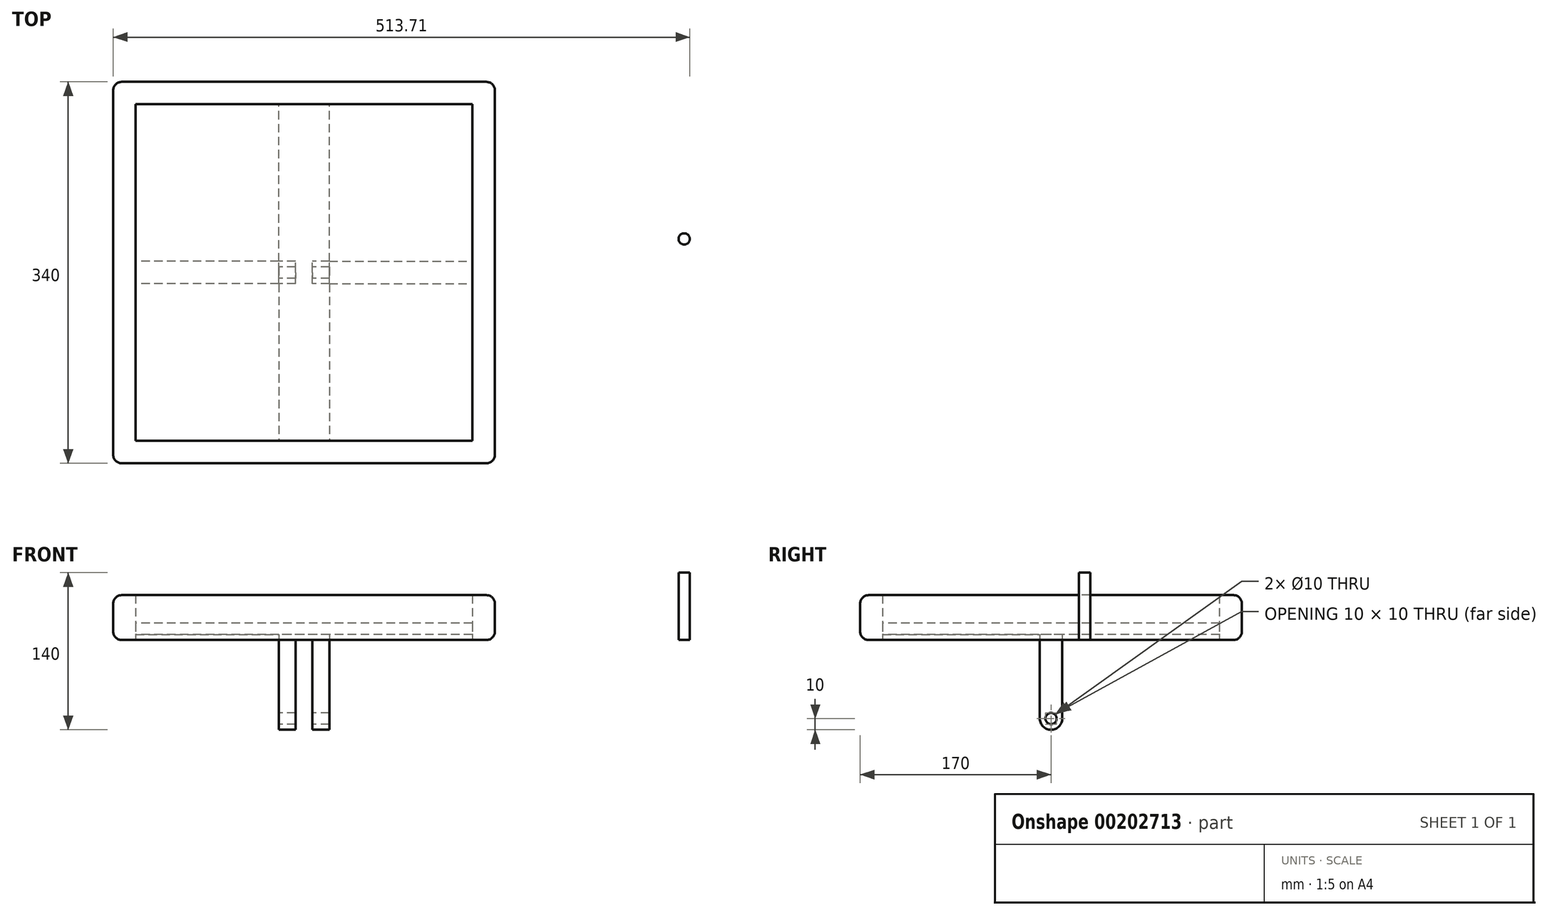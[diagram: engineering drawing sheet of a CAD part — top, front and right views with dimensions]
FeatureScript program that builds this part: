
annotation { "Feature Type Name" : "Feature", "Feature Type Description" : "" }
export const myFeature = defineFeature(function(context is Context, id is Id, definition is map)
    precondition{}
    {
        {
            var Q0;
            Q0=qCreatedBy(makeId("Top.planeOp"),FACE);
            var sketch = newSketch(context, id + "F0", { "sketchPlane" : qUnion([Q0])});
            skLineSegment(sketch, "E0.bottom", {"start": v(170, 170) * mm, "end": v(-170, 170) * mm});
            skLineSegment(sketch, "E0.top", {"start": v(170, -170) * mm, "end": v(-170, -170) * mm});
            skLineSegment(sketch, "E0.left", {"start": v(170, 170) * mm, "end": v(170, -170) * mm});
            skLineSegment(sketch, "E0.right", {"start": v(-170, 170) * mm, "end": v(-170, -170) * mm});
            skPoint(sketch, "E0.middle", {"position": v(0, 0) * mm});
            skLineSegment(sketch, "E1.bottom", {"start": v(150, 150) * mm, "end": v(-150, 150) * mm});
            skLineSegment(sketch, "E1.top", {"start": v(150, -150) * mm, "end": v(-150, -150) * mm});
            skLineSegment(sketch, "E1.left", {"start": v(150, 150) * mm, "end": v(150, -150) * mm});
            skLineSegment(sketch, "E1.right", {"start": v(-150, 150) * mm, "end": v(-150, -150) * mm});
            skCircle(sketch, "E2", {"center": v(338.71, 30.01) * mm, "radius": 5 * mm});
            skSolve(sketch);
        }
        {
            var Q0;
            Q0=makeQuery(id+"F0.imprint","IMPRINT",FACE,{"disambiguationData":[TD([[makeQuery(id+"F0.imprint","IMPRINT",EDGE,{"derivedFrom":sQuery(id+"F0.wireOp",EDGE,"E0.bottom")}),1.0]])]});
            extrude(context, id + "F1", {"entities" : qUnion([Q0]), "depth" : 40 * mm});
        }
        {
            var Q0;
            Q0=makeQuery(id+"F0.imprint","IMPRINT",FACE,{"disambiguationData":[TD([[makeQuery(id+"F0.imprint","IMPRINT",EDGE,{"derivedFrom":sQuery(id+"F0.wireOp",EDGE,"E1.bottom")}),1.0]])]});
            extrude(context, id + "F2", {"entities" : qUnion([Q0]), "operationType" : NewBodyOperationType.ADD, "depth" : 5 * mm});
        }
        {
            var Q0;
            Q0=makeQuery(id+"F0.imprint","IMPRINT",FACE,{"disambiguationData":[TD([[makeQuery(id+"F0.imprint","IMPRINT",EDGE,{"derivedFrom":sQuery(id+"F0.wireOp",EDGE,"E1.bottom")}),1.0]])]});
            var sketch = newSketch(context, id + "F3", { "sketchPlane" : qUnion([Q0])});
            skLineSegment(sketch, "E3.bottom", {"start": v(7.5, -10) * mm, "end": v(-7.5, -10) * mm});
            skLineSegment(sketch, "E3.top", {"start": v(7.5, 10) * mm, "end": v(-7.5, 10) * mm});
            skLineSegment(sketch, "E3.left", {"start": v(7.5, -10) * mm, "end": v(7.5, 10) * mm});
            skLineSegment(sketch, "E3.right", {"start": v(-7.5, -10) * mm, "end": v(-7.5, 10) * mm});
            skPoint(sketch, "E3.middle", {"position": v(0, 0) * mm});
            skLineSegment(sketch, "E4.bottom", {"start": v(22.5, -10) * mm, "end": v(-22.5, -10) * mm});
            skLineSegment(sketch, "E4.top", {"start": v(22.5, 10) * mm, "end": v(-22.5, 10) * mm});
            skLineSegment(sketch, "E4.left", {"start": v(22.5, -10) * mm, "end": v(22.5, 10) * mm});
            skLineSegment(sketch, "E4.right", {"start": v(-22.5, -10) * mm, "end": v(-22.5, 10) * mm});
            skLineSegment(sketch, "E5.bottom", {"start": v(-22.5, 10) * mm, "end": v(-150, 10) * mm});
            skLineSegment(sketch, "E5.top", {"start": v(-22.5, 150) * mm, "end": v(-150, 150) * mm});
            skLineSegment(sketch, "E5.left", {"start": v(-22.5, 10) * mm, "end": v(-22.5, 150) * mm});
            skLineSegment(sketch, "E5.right", {"start": v(-150, 10) * mm, "end": v(-150, 150) * mm});
            skLineSegment(sketch, "E6.bottom", {"start": v(22.5, 10) * mm, "end": v(150, 10) * mm});
            skLineSegment(sketch, "E6.top", {"start": v(22.5, 150) * mm, "end": v(150, 150) * mm});
            skLineSegment(sketch, "E6.left", {"start": v(22.5, 10) * mm, "end": v(22.5, 150) * mm});
            skLineSegment(sketch, "E6.right", {"start": v(150, 10) * mm, "end": v(150, 150) * mm});
            skLineSegment(sketch, "E7.bottom", {"start": v(22.5, -10) * mm, "end": v(150, -10) * mm});
            skLineSegment(sketch, "E7.top", {"start": v(22.5, -150) * mm, "end": v(150, -150) * mm});
            skLineSegment(sketch, "E7.left", {"start": v(22.5, -10) * mm, "end": v(22.5, -150) * mm});
            skLineSegment(sketch, "E7.right", {"start": v(150, -10) * mm, "end": v(150, -150) * mm});
            skLineSegment(sketch, "E8.bottom", {"start": v(-22.5, -10) * mm, "end": v(-150, -10) * mm});
            skLineSegment(sketch, "E8.top", {"start": v(-22.5, -150) * mm, "end": v(-150, -150) * mm});
            skLineSegment(sketch, "E8.left", {"start": v(-22.5, -10) * mm, "end": v(-22.5, -150) * mm});
            skLineSegment(sketch, "E8.right", {"start": v(-150, -10) * mm, "end": v(-150, -150) * mm});
            skSolve(sketch);
        }
        {
            var Q0;
            {var subQ0=sQuery(id+"F3.wireOp",EDGE,"E3.left");Q0=makeQuery(id+"F3.imprint","IMPRINT",FACE,{"disambiguationData":[TD([[makeQuery(id+"F3.imprint","IMPRINT",EDGE,{"derivedFrom":subQ0}),-1.0]])]});}
            var Q1;
            {var subQ0=sQuery(id+"F3.wireOp",EDGE,"E3.right");Q1=makeQuery(id+"F3.imprint","IMPRINT",FACE,{"disambiguationData":[TD([[makeQuery(id+"F3.imprint","IMPRINT",EDGE,{"derivedFrom":subQ0}),1.0]])]});}
            extrude(context, id + "F4", {"entities" : qUnion([Q0, Q1]), "operationType" : NewBodyOperationType.ADD, "oppositeDirection" : true, "depth" : 80 * mm});
        }
        {
            var Q0;
            {var subQ0=sQuery(id+"F3.wireOp",EDGE,"E4.bottom");Q0=makeQuery(id+"F4.opExtrude","CAP_EDGE",EDGE,{"disambiguationData":[OSD([subQ0]),TDD([makeQuery(id+"F3.imprint","IMPRINT",EDGE,{"disambiguationData":[TD([[makeQuery(id+"F3.imprint","INTERSECT",VERTEX,{"derivedFrom":[sQuery(id+"F3.wireOp",EDGE,"E3.right"),subQ0]}),-1.0]])],"derivedFrom":subQ0})])],"isStart":false});}
            var Q1;
            {var subQ0=sQuery(id+"F3.wireOp",EDGE,"E4.top");Q1=makeQuery(id+"F4.opExtrude","CAP_EDGE",EDGE,{"disambiguationData":[OSD([subQ0]),TDD([makeQuery(id+"F3.imprint","IMPRINT",EDGE,{"disambiguationData":[TD([[makeQuery(id+"F3.imprint","INTERSECT",VERTEX,{"derivedFrom":[sQuery(id+"F3.wireOp",EDGE,"E3.right"),subQ0]}),-1.0]])],"derivedFrom":subQ0})])],"isStart":false});}
            var Q2;
            {var subQ0=sQuery(id+"F3.wireOp",EDGE,"E4.bottom");Q2=makeQuery(id+"F4.opExtrude","CAP_EDGE",EDGE,{"disambiguationData":[OSD([subQ0]),TDD([makeQuery(id+"F3.imprint","IMPRINT",EDGE,{"disambiguationData":[TD([[makeQuery(id+"F3.imprint","INTERSECT",VERTEX,{"derivedFrom":[sQuery(id+"F3.wireOp",EDGE,"E3.left"),subQ0]}),1.0]])],"derivedFrom":subQ0})])],"isStart":false});}
            var Q3;
            {var subQ0=sQuery(id+"F3.wireOp",EDGE,"E4.top");Q3=makeQuery(id+"F4.opExtrude","CAP_EDGE",EDGE,{"disambiguationData":[OSD([subQ0]),TDD([makeQuery(id+"F3.imprint","IMPRINT",EDGE,{"disambiguationData":[TD([[makeQuery(id+"F3.imprint","INTERSECT",VERTEX,{"derivedFrom":[sQuery(id+"F3.wireOp",EDGE,"E3.left"),subQ0]}),1.0]])],"derivedFrom":subQ0})])],"isStart":false});}
            fillet(context, id + "F5", {"entities" : qUnion([Q0, Q1, Q2, Q3]), "radius" : 10 * mm, "tangentPropagation" : true, "allowEdgeOverflow" : false});
        }
        {
            var Q0;
            Q0=makeQuery(id+"F1.opExtrude","SWEPT_EDGE",EDGE,{"disambiguationData":[OSD([sQuery(id+"F0.wireOp",EDGE,"E0.top"),sQuery(id+"F0.wireOp",EDGE,"E0.right")])]});
            var Q1;
            Q1=makeQuery(id+"F1.opExtrude","SWEPT_EDGE",EDGE,{"disambiguationData":[OSD([sQuery(id+"F0.wireOp",EDGE,"E0.top"),sQuery(id+"F0.wireOp",EDGE,"E0.left")])]});
            var Q2;
            Q2=makeQuery(id+"F1.opExtrude","SWEPT_EDGE",EDGE,{"disambiguationData":[OSD([sQuery(id+"F0.wireOp",EDGE,"E0.bottom"),sQuery(id+"F0.wireOp",EDGE,"E0.right")])]});
            var Q3;
            Q3=makeQuery(id+"F1.opExtrude","CAP_EDGE",EDGE,{"disambiguationData":[OSD([sQuery(id+"F0.wireOp",EDGE,"E0.bottom")])],"isStart":true});
            var Q4;
            Q4=makeQuery(id+"F1.opExtrude","CAP_EDGE",EDGE,{"disambiguationData":[OSD([sQuery(id+"F0.wireOp",EDGE,"E0.left")])],"isStart":true});
            var Q5;
            Q5=makeQuery(id+"F1.opExtrude","SWEPT_EDGE",EDGE,{"disambiguationData":[OSD([sQuery(id+"F0.wireOp",EDGE,"E0.bottom"),sQuery(id+"F0.wireOp",EDGE,"E0.left")])]});
            var Q6;
            Q6=makeQuery(id+"F1.opExtrude","CAP_EDGE",EDGE,{"disambiguationData":[OSD([sQuery(id+"F0.wireOp",EDGE,"E0.left")])],"isStart":false});
            var Q7;
            Q7=makeQuery(id+"F1.opExtrude","CAP_EDGE",EDGE,{"disambiguationData":[OSD([sQuery(id+"F0.wireOp",EDGE,"E0.top")])],"isStart":false});
            var Q8;
            Q8=makeQuery(id+"F1.opExtrude","CAP_EDGE",EDGE,{"disambiguationData":[OSD([sQuery(id+"F0.wireOp",EDGE,"E0.top")])],"isStart":true});
            var Q9;
            Q9=makeQuery(id+"F1.opExtrude","CAP_EDGE",EDGE,{"disambiguationData":[OSD([sQuery(id+"F0.wireOp",EDGE,"E0.right")])],"isStart":false});
            var Q10;
            Q10=makeQuery(id+"F1.opExtrude","CAP_EDGE",EDGE,{"disambiguationData":[OSD([sQuery(id+"F0.wireOp",EDGE,"E0.right")])],"isStart":true});
            var Q11;
            Q11=makeQuery(id+"F1.opExtrude","CAP_EDGE",EDGE,{"disambiguationData":[OSD([sQuery(id+"F0.wireOp",EDGE,"E0.bottom")])],"isStart":false});
            fillet(context, id + "F6", {"entities" : qUnion([Q0, Q1, Q2, Q3, Q4, Q5, Q6, Q7, Q8, Q9, Q10, Q11]), "radius" : 7.5 * mm, "tangentPropagation" : true, "allowEdgeOverflow" : false});
        }
        {
            var Q0;
            Q0=makeQuery(id+"F4.opExtrude","SWEPT_FACE",FACE,{"disambiguationData":[OSD([sQuery(id+"F3.wireOp",EDGE,"E4.right")])]});
            var sketch = newSketch(context, id + "F7", { "sketchPlane" : qUnion([Q0])});
            skCircle(sketch, "E9", {"center": v(0, -70) * mm, "radius": 5 * mm});
            skSolve(sketch);
        }
        {
            var Q0;
            Q0=makeQuery(id+"F7.imprint","IMPRINT",FACE,{"disambiguationData":[TD([[makeQuery(id+"F7.imprint","IMPRINT",EDGE,{"derivedFrom":sQuery(id+"F7.wireOp",EDGE,"E9")}),1.0]])]});
            extrude(context, id + "F8", {"entities" : qUnion([Q0]), "oppositeDirection" : true, "depth" : 45 * mm});
        }
        {
            var Q0;
            Q0=makeQuery(id+"F8.opExtrude","SWEPT_BODY",BODY,{"disambiguationData":[OSD([sQuery(id+"F7.wireOp",EDGE,"E9")])]});
            var Q1;
            Q1=makeQuery(id+"F1.opExtrude","SWEPT_BODY",BODY,{"disambiguationData":[OSD([sQuery(id+"F0.wireOp",EDGE,"E0.bottom"),sQuery(id+"F0.wireOp",EDGE,"E0.top"),sQuery(id+"F0.wireOp",EDGE,"E0.left"),sQuery(id+"F0.wireOp",EDGE,"E0.right"),sQuery(id+"F0.wireOp",EDGE,"E1.bottom"),sQuery(id+"F0.wireOp",EDGE,"E1.top"),sQuery(id+"F0.wireOp",EDGE,"E1.left"),sQuery(id+"F0.wireOp",EDGE,"E1.right")])]});
            booleanBodies(context, id + "F9", {"operationType" : BooleanOperationType.SUBTRACTION, "tools" : qUnion([Q0]), "targets" : qUnion([Q1])});
        }
        {
            var Q0;
            Q0=makeQuery(id+"F0.imprint","IMPRINT",FACE,{"disambiguationData":[TD([[makeQuery(id+"F0.imprint","IMPRINT",EDGE,{"derivedFrom":sQuery(id+"F0.wireOp",EDGE,"E2")}),1.0]])]});
            extrude(context, id + "F10", {"entities" : qUnion([Q0]), "depth" : 60 * mm});
        }
        {
            var Q0;
            Q0=makeQuery(id+"F3.imprint","IMPRINT",FACE,{"disambiguationData":[TD([[makeQuery(id+"F3.imprint","IMPRINT",EDGE,{"derivedFrom":sQuery(id+"F3.wireOp",EDGE,"E5.bottom")}),-1.0]])]});
            var Q1;
            Q1=makeQuery(id+"F3.imprint","IMPRINT",FACE,{"disambiguationData":[TD([[makeQuery(id+"F3.imprint","IMPRINT",EDGE,{"derivedFrom":sQuery(id+"F3.wireOp",EDGE,"E6.bottom")}),1.0]])]});
            var Q2;
            Q2=makeQuery(id+"F3.imprint","IMPRINT",FACE,{"disambiguationData":[TD([[makeQuery(id+"F3.imprint","IMPRINT",EDGE,{"derivedFrom":sQuery(id+"F3.wireOp",EDGE,"E7.bottom")}),-1.0]])]});
            var Q3;
            Q3=makeQuery(id+"F3.imprint","IMPRINT",FACE,{"disambiguationData":[TD([[makeQuery(id+"F3.imprint","IMPRINT",EDGE,{"derivedFrom":sQuery(id+"F3.wireOp",EDGE,"E8.bottom")}),1.0]])]});
            extrude(context, id + "F11", {"entities" : qUnion([Q0, Q1, Q2, Q3]), "operationType" : NewBodyOperationType.REMOVE, "endBound" : BoundingType.THROUGH_ALL, "depth" : 25 * mm});
        }
        {
            var Q0;
            Q0=makeQuery(id+"F2.opExtrude","CAP_FACE",FACE,{"disambiguationData":[OSD([sQuery(id+"F0.wireOp",EDGE,"E1.bottom"),sQuery(id+"F0.wireOp",EDGE,"E1.top"),sQuery(id+"F0.wireOp",EDGE,"E1.left"),sQuery(id+"F0.wireOp",EDGE,"E1.right")])],"isStart":false});
            var sketch = newSketch(context, id + "F12", { "sketchPlane" : qUnion([Q0])});
            skLineSegment(sketch, "E10.bottom", {"start": v(150, 150) * mm, "end": v(-150, 150) * mm});
            skLineSegment(sketch, "E10.top", {"start": v(150, -150) * mm, "end": v(-150, -150) * mm});
            skLineSegment(sketch, "E10.left", {"start": v(150, 150) * mm, "end": v(150, -150) * mm});
            skLineSegment(sketch, "E10.right", {"start": v(-150, 150) * mm, "end": v(-150, -150) * mm});
            skPoint(sketch, "E10.middle", {"position": v(0, 0) * mm});
            skSolve(sketch);
        }
        {
            var Q0;
            {var subQ1=makeQuery(id+"F2.opExtrude","CAP_FACE",FACE,{"disambiguationData":[OSD([sQuery(id+"F0.wireOp",EDGE,"E1.bottom"),sQuery(id+"F0.wireOp",EDGE,"E1.top"),sQuery(id+"F0.wireOp",EDGE,"E1.left"),sQuery(id+"F0.wireOp",EDGE,"E1.right")])],"isStart":false});var subQ5=makeQuery(id+"F11.boolean.opBoolean","INTERSECT",EDGE,{"derivedFrom":[subQ1,makeQuery(id+"F11.opExtrude","SWEPT_FACE",FACE,{"disambiguationData":[OSD([sQuery(id+"F3.wireOp",EDGE,"E8.bottom")])]})]});Q0=makeQuery(id+"F12.imprint","IMPRINT",FACE,{"disambiguationData":[TD([[makeQuery(id+"F12.imprint","IMPRINT",EDGE,{"derivedFrom":subQ5}),-1.0]])]});}
            var Q1;
            {var subQ0=makeQuery(id+"F2.opExtrude","CAP_FACE",FACE,{"disambiguationData":[OSD([sQuery(id+"F0.wireOp",EDGE,"E1.bottom"),sQuery(id+"F0.wireOp",EDGE,"E1.top"),sQuery(id+"F0.wireOp",EDGE,"E1.left"),sQuery(id+"F0.wireOp",EDGE,"E1.right")])],"isStart":false});var subQ2=makeQuery(id+"F11.boolean.opBoolean","INTERSECT",EDGE,{"derivedFrom":[subQ0,makeQuery(id+"F11.opExtrude","SWEPT_FACE",FACE,{"disambiguationData":[OSD([sQuery(id+"F3.wireOp",EDGE,"E5.bottom")])]})]});Q1=makeQuery(id+"F12.imprint","IMPRINT",FACE,{"disambiguationData":[TD([[makeQuery(id+"F12.imprint","IMPRINT",EDGE,{"derivedFrom":subQ2}),-1.0]])]});}
            var Q2;
            {var subQ1=makeQuery(id+"F2.opExtrude","CAP_FACE",FACE,{"disambiguationData":[OSD([sQuery(id+"F0.wireOp",EDGE,"E1.bottom"),sQuery(id+"F0.wireOp",EDGE,"E1.top"),sQuery(id+"F0.wireOp",EDGE,"E1.left"),sQuery(id+"F0.wireOp",EDGE,"E1.right")])],"isStart":false});var subQ5=makeQuery(id+"F11.boolean.opBoolean","INTERSECT",EDGE,{"derivedFrom":[subQ1,makeQuery(id+"F11.opExtrude","SWEPT_FACE",FACE,{"disambiguationData":[OSD([sQuery(id+"F3.wireOp",EDGE,"E5.bottom")])]})]});Q2=makeQuery(id+"F12.imprint","IMPRINT",FACE,{"disambiguationData":[TD([[makeQuery(id+"F12.imprint","IMPRINT",EDGE,{"derivedFrom":subQ5}),1.0]])]});}
            var Q3;
            {var subQ1=makeQuery(id+"F2.opExtrude","CAP_FACE",FACE,{"disambiguationData":[OSD([sQuery(id+"F0.wireOp",EDGE,"E1.bottom"),sQuery(id+"F0.wireOp",EDGE,"E1.top"),sQuery(id+"F0.wireOp",EDGE,"E1.left"),sQuery(id+"F0.wireOp",EDGE,"E1.right")])],"isStart":false});var subQ5=makeQuery(id+"F11.boolean.opBoolean","INTERSECT",EDGE,{"derivedFrom":[subQ1,makeQuery(id+"F11.opExtrude","SWEPT_FACE",FACE,{"disambiguationData":[OSD([sQuery(id+"F3.wireOp",EDGE,"E6.bottom")])]})]});Q3=makeQuery(id+"F12.imprint","IMPRINT",FACE,{"disambiguationData":[TD([[makeQuery(id+"F12.imprint","IMPRINT",EDGE,{"derivedFrom":subQ5}),-1.0]])]});}
            var Q4;
            {var subQ1=makeQuery(id+"F2.opExtrude","CAP_FACE",FACE,{"disambiguationData":[OSD([sQuery(id+"F0.wireOp",EDGE,"E1.bottom"),sQuery(id+"F0.wireOp",EDGE,"E1.top"),sQuery(id+"F0.wireOp",EDGE,"E1.left"),sQuery(id+"F0.wireOp",EDGE,"E1.right")])],"isStart":false});var subQ5=makeQuery(id+"F11.boolean.opBoolean","INTERSECT",EDGE,{"derivedFrom":[subQ1,makeQuery(id+"F11.opExtrude","SWEPT_FACE",FACE,{"disambiguationData":[OSD([sQuery(id+"F3.wireOp",EDGE,"E7.bottom")])]})]});Q4=makeQuery(id+"F12.imprint","IMPRINT",FACE,{"disambiguationData":[TD([[makeQuery(id+"F12.imprint","IMPRINT",EDGE,{"derivedFrom":subQ5}),1.0]])]});}
            extrude(context, id + "F13", {"entities" : qUnion([Q0, Q1, Q2, Q3, Q4]), "depth" : 10 * mm});
        }
    });
